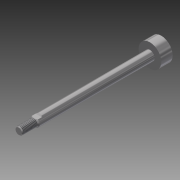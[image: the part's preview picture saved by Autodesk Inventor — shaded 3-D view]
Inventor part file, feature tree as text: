
AUTODESK INVENTOR PART (.ipt)
format: ipt  version: 2016 SP1 (Build 200210100, 210)  size: 113,152 bytes
history: native  units: in
note: dims shown in document units (in); Inventor stores cm internally (conversion verified against a paired STEP export)
features: other x7, sketch x3, extrude x2, revolve x1, thread x1
ambient origin geometry x8: Origin, YZ Plane, XZ Plane, XY Plane, X Axis, Y Axis, Z Axis, Center Point
bodies: Solid1 (feature_tree)
feature tree (14):
  revolve  "Revolution1"  [1 undecoded]
  thread  "Thread1"  [1 undecoded]
  extrude  "Extrusion1"  TaperAngle=0.0deg  [1 undecoded]
  extrude  "Extrusion2"  [1 undecoded]
  other  "conn_XY"
  other  "conn_YZ"
  other  "conn_ZX"
  other  "conn_X"
  other  "conn_Y"
  other  "conn_Z"
  other  "conn_Center"
  sketch  "Sketch_1"  dims[d0=360.0deg d1=0.4787in d2=0.0in d3=0.63in d4=0.0in]
  sketch  "Sketch_2"  dims[d5=0.63in d6=0.0in d7=0.0in]
  sketch  "Sketch_3"
note: 4 required parameter values undecoded (feature->parameter linkage not recoverable at this tier; creation-order binding heuristic only, values carry confidence <= 0.55)